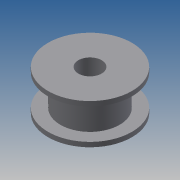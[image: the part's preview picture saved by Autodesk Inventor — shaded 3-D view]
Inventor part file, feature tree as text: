
AUTODESK INVENTOR PART (.ipt)
format: ipt  version: 2013 (Build 170138000, 138)  size: 97,280 bytes
history: native  units: mm
features: extrude x4, sketch x4, projected_geometry x1
ambient origin geometry x8: Origin, YZ Plane, XZ Plane, XY Plane, X Axis, Y Axis, Z Axis, Center Point
bodies: Solid1 (feature_tree)
feature tree (9):
  extrude  "Extrusion1"  Depth=8.6mm TaperAngle=0.0deg
  extrude  "Extrusion2"  Depth=1.0mm TaperAngle=0.0deg
  extrude  "Extrusion3"  Depth=5.0mm
  extrude  "Extrusion4"  [1 undecoded]
  sketch  "Sketch1"  dims[d0=12.732395mm d3=8.6mm d4=0.0mm]
  sketch  "Sketch2"  dims[d5=18.0mm d7=1.0mm d8=0.0mm]
  sketch  "Sketch3"  dims[d9=1.0mm d10=0.0mm d11=5.0mm]
  projected_geometry  "Projected Loop1"
  sketch  "Sketch4"  dims[d13=1.0mm d14=0.0mm]
note: 1 required parameter value undecoded (feature->parameter linkage not recoverable at this tier; creation-order binding heuristic only, values carry confidence <= 0.55)
